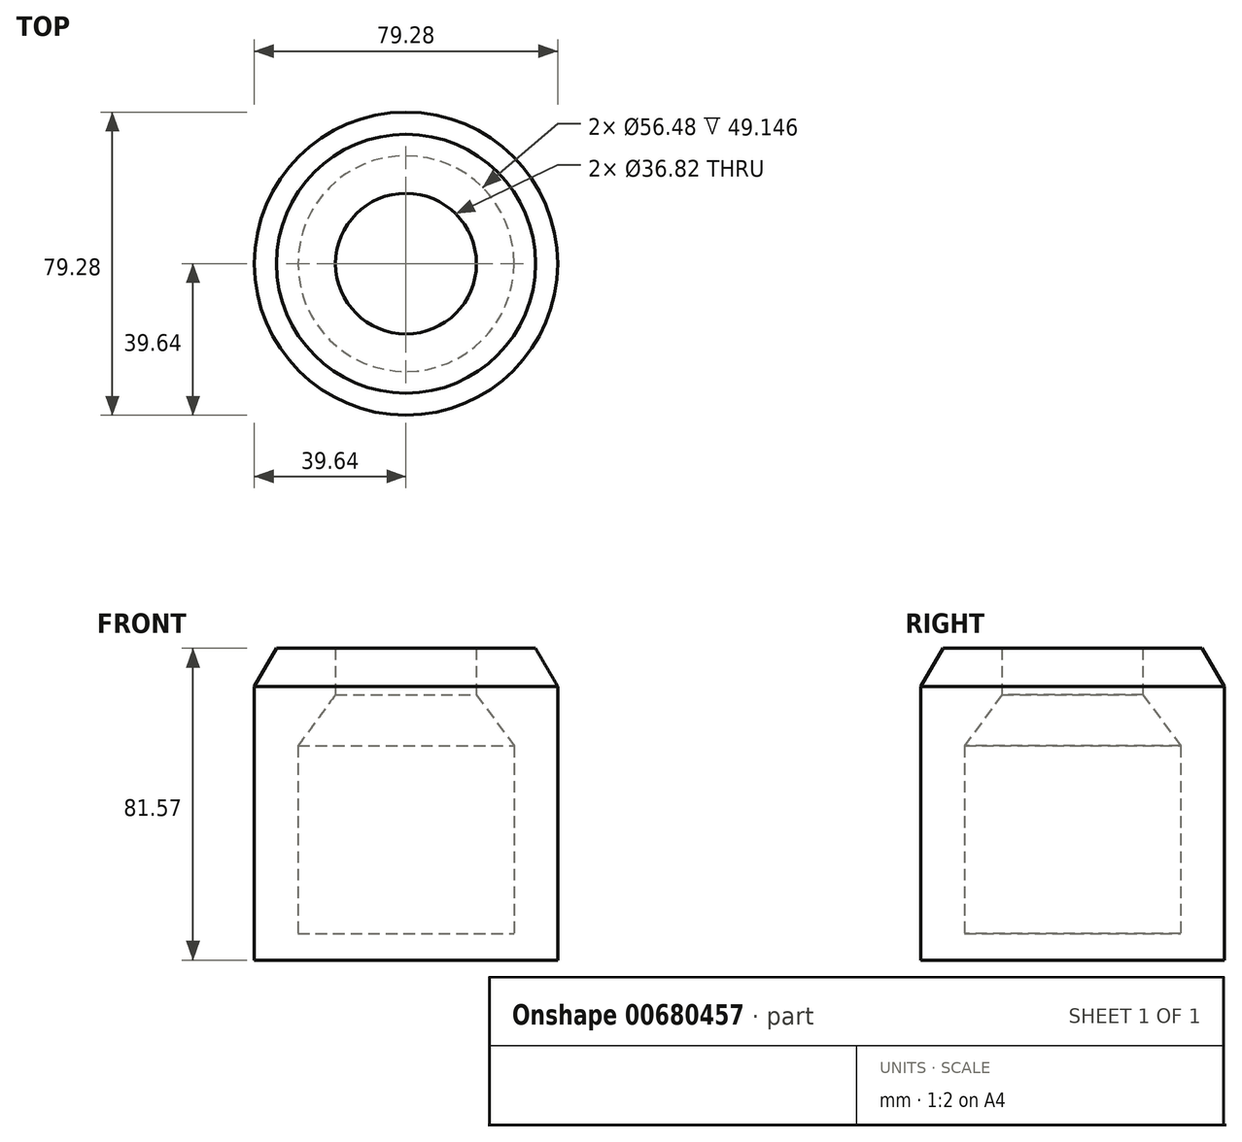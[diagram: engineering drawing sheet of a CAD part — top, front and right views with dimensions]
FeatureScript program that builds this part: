
annotation { "Feature Type Name" : "Feature", "Feature Type Description" : "" }
export const myFeature = defineFeature(function(context is Context, id is Id, definition is map)
    precondition{}
    {
        {
            var Q0;
            Q0=qCreatedBy(makeId("Front.planeOp"),FACE);
            var sketch = newSketch(context, id + "F0", { "sketchPlane" : qUnion([Q0])});
            skLineSegment(sketch, "E0", {"start": v(-39.64, 43.26) * mm, "end": v(-39.64, -38.3) * mm});
            skLineSegment(sketch, "E1", {"start": v(-39.64, -38.3) * mm, "end": v(0, -38.3) * mm});
            skLineSegment(sketch, "E2", {"start": v(0, -38.3) * mm, "end": v(0, -31.4) * mm});
            skLineSegment(sketch, "E3", {"start": v(0, -31.4) * mm, "end": v(-28.24, -31.4) * mm});
            skLineSegment(sketch, "E4", {"start": v(-28.24, -31.4) * mm, "end": v(-28.24, 17.74) * mm});
            skLineSegment(sketch, "E5", {"start": v(-28.24, 17.74) * mm, "end": v(-18.41, 31.15) * mm});
            skLineSegment(sketch, "E6", {"start": v(-18.41, 31.15) * mm, "end": v(-18.41, 43.26) * mm});
            skLineSegment(sketch, "E7", {"start": v(-39.64, 43.26) * mm, "end": v(-18.41, 43.26) * mm});
            skSolve(sketch);
        }
        {
            var Q0;
            Q0=makeQuery(id+"F0.imprint","IMPRINT",FACE,{"disambiguationData":[TD([[makeQuery(id+"F0.imprint","IMPRINT",EDGE,{"derivedFrom":sQuery(id+"F0.wireOp",EDGE,"E0")}),1.0]])]});
            var Q1;
            Q1=sQuery(id+"F0.wireOp",EDGE,"E2");
            revolve(context, id + "F1", {"entities" : qUnion([Q0]), "axis" : qUnion([Q1]), "revolveType" : RevolveType.FULL});
        }
        {
            var Q0;
            Q0=makeQuery(id+"F1.opRevolve","SWEPT_EDGE",EDGE,{"disambiguationData":[OSD([sQuery(id+"F0.wireOp",EDGE,"E0"),sQuery(id+"F0.wireOp",EDGE,"E7")])]});
            chamfer(context, id + "F2", {"entities" : qUnion([Q0]), "chamferType" : ChamferType.OFFSET_ANGLE, "width" : 10 * mm, "oppositeDirection" : false, "angle" : 30 * degree, "tangentPropagation" : true});
        }
    });
